# Revit family: Gira_027130
name_source: partatom
category: Electrical Fixtures
revit_build: Autodesk Revit 2017 (Build: 20160225_1515(x64)
units: mm (PartAtom-declared; Revit-internal decimal feet)

## family parameters
Cut with Voids When Loaded = No
Host = Face
Maintain Annotation Orientation = Yes
Part Type = Normal
Room Calculation Point = No
Round Connector Dimension = Use Diameter
Shared = No

## types (1)
- Hous. centre ins. in.sp. btns Ø 22.5mm WP surface-mounted grey
    Assembly arrangement = Basic element with complete housing
    Available = No
    BIM (1) = https://media.stage.bim.site und Tasten.rfa?public/gira/36a6b08/IP44_Komplettgerät_Schalten und Tasten.rfa
    Category = Insert/cover for communication technology
    Colour = Grey
    Data sheet (1) = https://katalog.gira.de
    Default Elevation = 1219 mm
    Description = Hous.cent.in.sp.btns D22.5mm WP SM GY,Housing with yellow centre insert and inscription space; accepts push-buttons and mushroom buttons ( 22.5 mm diameter),,yellow,Features:,- For emergency stop or emergency off.
    GTIN = 4010337271307
    HAN = 027130
    Halogen free = Yes
    HeinzeBIM = https://bimportal.heinze.de
    Imprintable label = With indication plate
    Luster terminal = No
    Manufacturer = Gira
    Manufacturer URL = https://www.gira.de
    Material = Plastic
    Material quality = Other
    Mounting method = Surface mounted (plaster)
    Name = Hous. centre ins. in.sp. btns Ø 22.5mm WP surface-mounted grey
    Suitable for degree of protection (IP) = IP44
    Support ring = Yes
    Surface finishing = Not applicable
    Surface protection = Other
    Transparent = No
    Type of fastening = Mounting with claw and screw
    URL = http://katalog.gira.de
    Utilization = Other
    With dust cover = No
    With hinged lid = No
    With imprint = No
    With strain relief = No

## geometry (parser evidence)
native form markers: Sweep x3
no freeform markers — native parametric forms only
